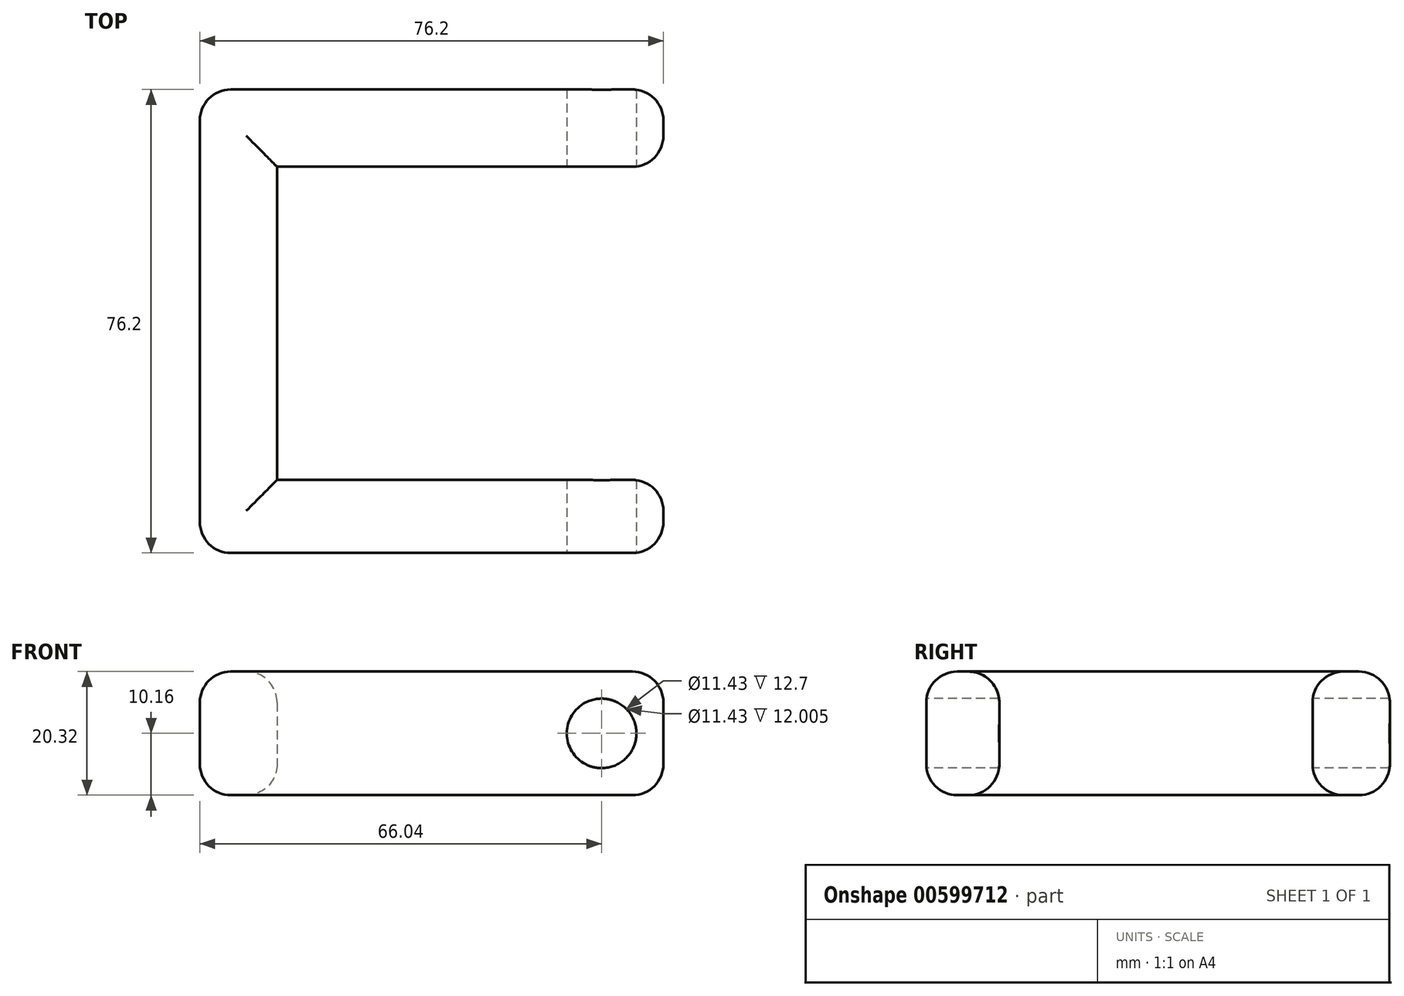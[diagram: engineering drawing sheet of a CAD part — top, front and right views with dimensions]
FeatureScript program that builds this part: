
annotation { "Feature Type Name" : "Feature", "Feature Type Description" : "" }
export const myFeature = defineFeature(function(context is Context, id is Id, definition is map)
    precondition{}
    {
        {
            var Q0;
            Q0=qCreatedBy(makeId("Top.planeOp"),FACE);
            var sketch = newSketch(context, id + "F0", { "sketchPlane" : qUnion([Q0])});
            skLineSegment(sketch, "E0", {"start": v(0, 0) * mm, "end": v(-76.2, 0) * mm});
            skLineSegment(sketch, "E1", {"start": v(-76.2, 0) * mm, "end": v(-76.2, 76.2) * mm});
            skLineSegment(sketch, "E2", {"start": v(-76.2, 76.2) * mm, "end": v(0, 76.2) * mm});
            skLineSegment(sketch, "E3", {"start": v(0, 76.2) * mm, "end": v(0, 63.5) * mm});
            skLineSegment(sketch, "E4", {"start": v(0, 63.5) * mm, "end": v(-63.5, 63.5) * mm});
            skLineSegment(sketch, "E5", {"start": v(-63.5, 63.5) * mm, "end": v(-63.5, 12) * mm});
            skLineSegment(sketch, "E6", {"start": v(-63.5, 12) * mm, "end": v(0, 12) * mm});
            skLineSegment(sketch, "E7", {"start": v(0, 12) * mm, "end": v(0, 0) * mm});
            skSolve(sketch);
        }
        {
            var Q0;
            Q0=makeQuery(id+"F0.imprint","IMPRINT",FACE,{"disambiguationData":[TD([[makeQuery(id+"F0.imprint","IMPRINT",EDGE,{"derivedFrom":sQuery(id+"F0.wireOp",EDGE,"E0")}),-1.0]])]});
            extrude(context, id + "F1", {"entities" : qUnion([Q0]), "depth" : 20.32 * mm, "offsetDistance" : 25.4 * mm});
        }
        {
            var Q0;
            Q0=makeQuery(id+"F1.opExtrude","SWEPT_FACE",FACE,{"disambiguationData":[OSD([sQuery(id+"F0.wireOp",EDGE,"E0")])]});
            var sketch = newSketch(context, id + "F2", { "sketchPlane" : qUnion([Q0])});
            skCircle(sketch, "E8", {"center": v(-10.16, 10.16) * mm, "radius": 5.72 * mm});
            skSolve(sketch);
        }
        {
            var Q0;
            Q0 = qSketchRegion(id + "F2", true);
            extrude(context, id + "F3", {"entities" : qUnion([Q0]), "operationType" : NewBodyOperationType.REMOVE, "oppositeDirection" : true, "depth" : 863.6 * mm, "offsetDistance" : 25.4 * mm});
        }
        {
            var Q0;
            Q0=makeQuery(id+"F1.opExtrude","CAP_EDGE",EDGE,{"disambiguationData":[OSD([sQuery(id+"F0.wireOp",EDGE,"E2")])],"isStart":true});
            var Q1;
            Q1=makeQuery(id+"F1.opExtrude","CAP_EDGE",EDGE,{"disambiguationData":[OSD([sQuery(id+"F0.wireOp",EDGE,"E4")])],"isStart":true});
            var Q2;
            Q2=makeQuery(id+"F1.opExtrude","CAP_EDGE",EDGE,{"disambiguationData":[OSD([sQuery(id+"F0.wireOp",EDGE,"E4")])],"isStart":false});
            var Q3;
            Q3=makeQuery(id+"F1.opExtrude","CAP_EDGE",EDGE,{"disambiguationData":[OSD([sQuery(id+"F0.wireOp",EDGE,"E2")])],"isStart":false});
            var Q4;
            Q4=makeQuery(id+"F1.opExtrude","CAP_EDGE",EDGE,{"disambiguationData":[OSD([sQuery(id+"F0.wireOp",EDGE,"E5")])],"isStart":false});
            var Q5;
            Q5=makeQuery(id+"F1.opExtrude","CAP_EDGE",EDGE,{"disambiguationData":[OSD([sQuery(id+"F0.wireOp",EDGE,"E1")])],"isStart":false});
            var Q6;
            Q6=makeQuery(id+"F1.opExtrude","CAP_EDGE",EDGE,{"disambiguationData":[OSD([sQuery(id+"F0.wireOp",EDGE,"E5")])],"isStart":true});
            var Q7;
            Q7=makeQuery(id+"F1.opExtrude","SWEPT_FACE",FACE,{"disambiguationData":[OSD([sQuery(id+"F0.wireOp",EDGE,"E1")])]});
            var Q8;
            Q8=makeQuery(id+"F1.opExtrude","CAP_EDGE",EDGE,{"disambiguationData":[OSD([sQuery(id+"F0.wireOp",EDGE,"E0")])],"isStart":true});
            var Q9;
            Q9=makeQuery(id+"F1.opExtrude","CAP_EDGE",EDGE,{"disambiguationData":[OSD([sQuery(id+"F0.wireOp",EDGE,"E0")])],"isStart":false});
            var Q10;
            Q10=makeQuery(id+"F1.opExtrude","CAP_EDGE",EDGE,{"disambiguationData":[OSD([sQuery(id+"F0.wireOp",EDGE,"E6")])],"isStart":true});
            var Q11;
            Q11=makeQuery(id+"F1.opExtrude","CAP_EDGE",EDGE,{"disambiguationData":[OSD([sQuery(id+"F0.wireOp",EDGE,"E6")])],"isStart":false});
            var Q12;
            Q12=makeQuery(id+"F1.opExtrude","SWEPT_FACE",FACE,{"disambiguationData":[OSD([sQuery(id+"F0.wireOp",EDGE,"E3")])]});
            var Q13;
            Q13=makeQuery(id+"F1.opExtrude","SWEPT_FACE",FACE,{"disambiguationData":[OSD([sQuery(id+"F0.wireOp",EDGE,"E7")])]});
            fillet(context, id + "F4", {"entities" : qUnion([Q0, Q1, Q2, Q3, Q4, Q5, Q6, Q7, Q8, Q9, Q10, Q11, Q12, Q13]), "radius" : 5.08 * mm, "tangentPropagation" : true, "allowEdgeOverflow" : false});
        }
    });
